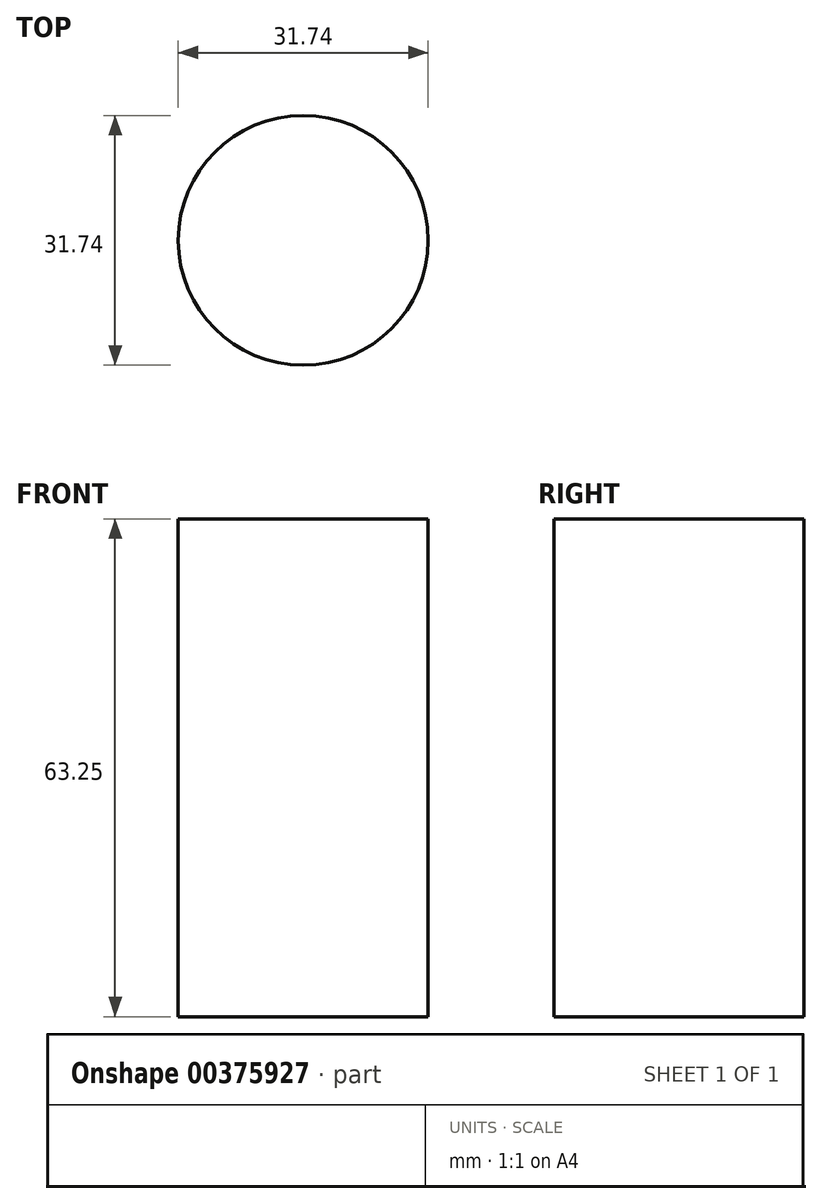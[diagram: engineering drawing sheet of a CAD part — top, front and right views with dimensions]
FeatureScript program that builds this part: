
annotation { "Feature Type Name" : "Feature", "Feature Type Description" : "" }
export const myFeature = defineFeature(function(context is Context, id is Id, definition is map)
    precondition{}
    {
        {
            var Q0;
            Q0=qCreatedBy(makeId("Top.planeOp"),FACE);
            var sketch = newSketch(context, id + "F0", { "sketchPlane" : qUnion([Q0])});
            skCircle(sketch, "E0", {"center": v(0, 0) * mm, "radius": 15.87 * mm});
            skSolve(sketch);
        }
        {
            var Q0;
            Q0 = qSketchRegion(id + "F0", true);
            extrude(context, id + "F1", {"entities" : qUnion([Q0]), "depth" : 63.25 * mm});
        }
        {
            var Q0;
            Q0=makeQuery(id+"F1.opExtrude","SWEPT_BODY",BODY,{"disambiguationData":[OSD([sQuery(id+"F0.wireOp",EDGE,"E0")])]});
            var Q1;
            Q1=makeQuery(id+"F1.opExtrude","SWEPT_FACE",FACE,{"disambiguationData":[OSD([sQuery(id+"F0.wireOp",EDGE,"E0")])]});
            circularPattern(context, id + "F2", {"entities" : qUnion([Q0]), "axis" : qUnion([Q1]), "angle" : 72 * degree, "instanceCount" : 5, "equalSpace" : true});
        }
    });
